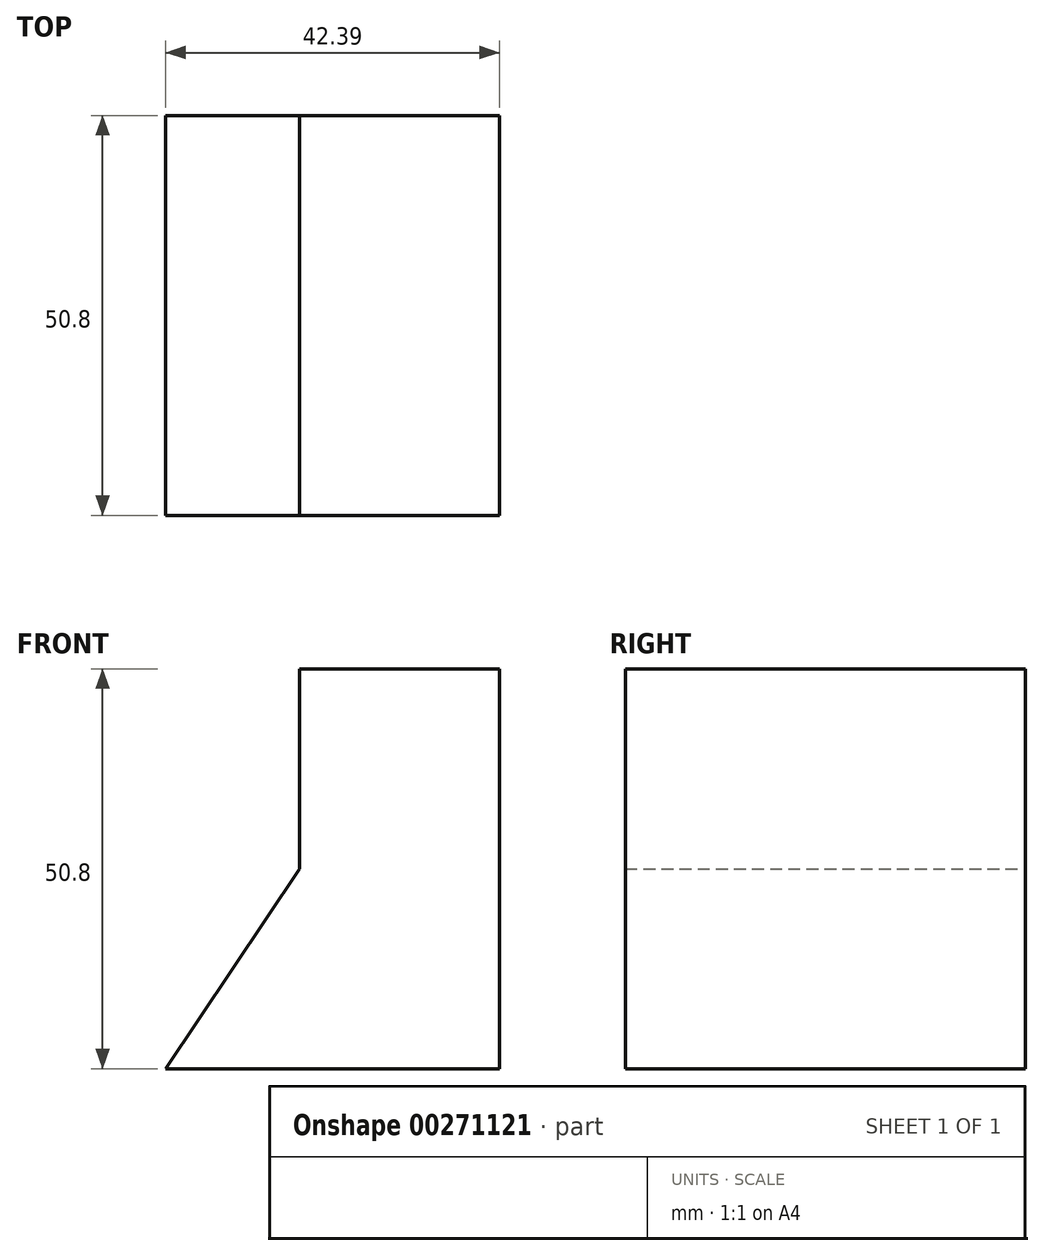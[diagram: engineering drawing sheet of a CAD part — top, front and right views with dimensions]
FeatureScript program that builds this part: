
annotation { "Feature Type Name" : "Feature", "Feature Type Description" : "" }
export const myFeature = defineFeature(function(context is Context, id is Id, definition is map)
    precondition{}
    {
        {
            var Q0;
            Q0=qCreatedBy(makeId("Front.planeOp"),FACE);
            var sketch = newSketch(context, id + "F0", { "sketchPlane" : qUnion([Q0])});
            skLineSegment(sketch, "E0", {"start": v(0, 0) * mm, "end": v(0, 50.8) * mm});
            skLineSegment(sketch, "E1", {"start": v(0, 50.8) * mm, "end": v(-25.4, 50.8) * mm});
            skLineSegment(sketch, "E2", {"start": v(-25.4, 50.8) * mm, "end": v(-25.4, 25.4) * mm});
            skLineSegment(sketch, "E3", {"start": v(-25.4, 25.4) * mm, "end": v(-42.4, 0) * mm});
            skLineSegment(sketch, "E4", {"start": v(-42.4, 0) * mm, "end": v(0, 0) * mm});
            skSolve(sketch);
        }
        {
            var Q0;
            Q0=makeQuery(id+"F0.imprint","IMPRINT",FACE,{"disambiguationData":[TD([[makeQuery(id+"F0.imprint","IMPRINT",EDGE,{"derivedFrom":sQuery(id+"F0.wireOp",EDGE,"E0")}),1.0]])]});
            extrude(context, id + "F1", {"entities" : qUnion([Q0]), "depth" : 50.8 * mm});
        }
    });
